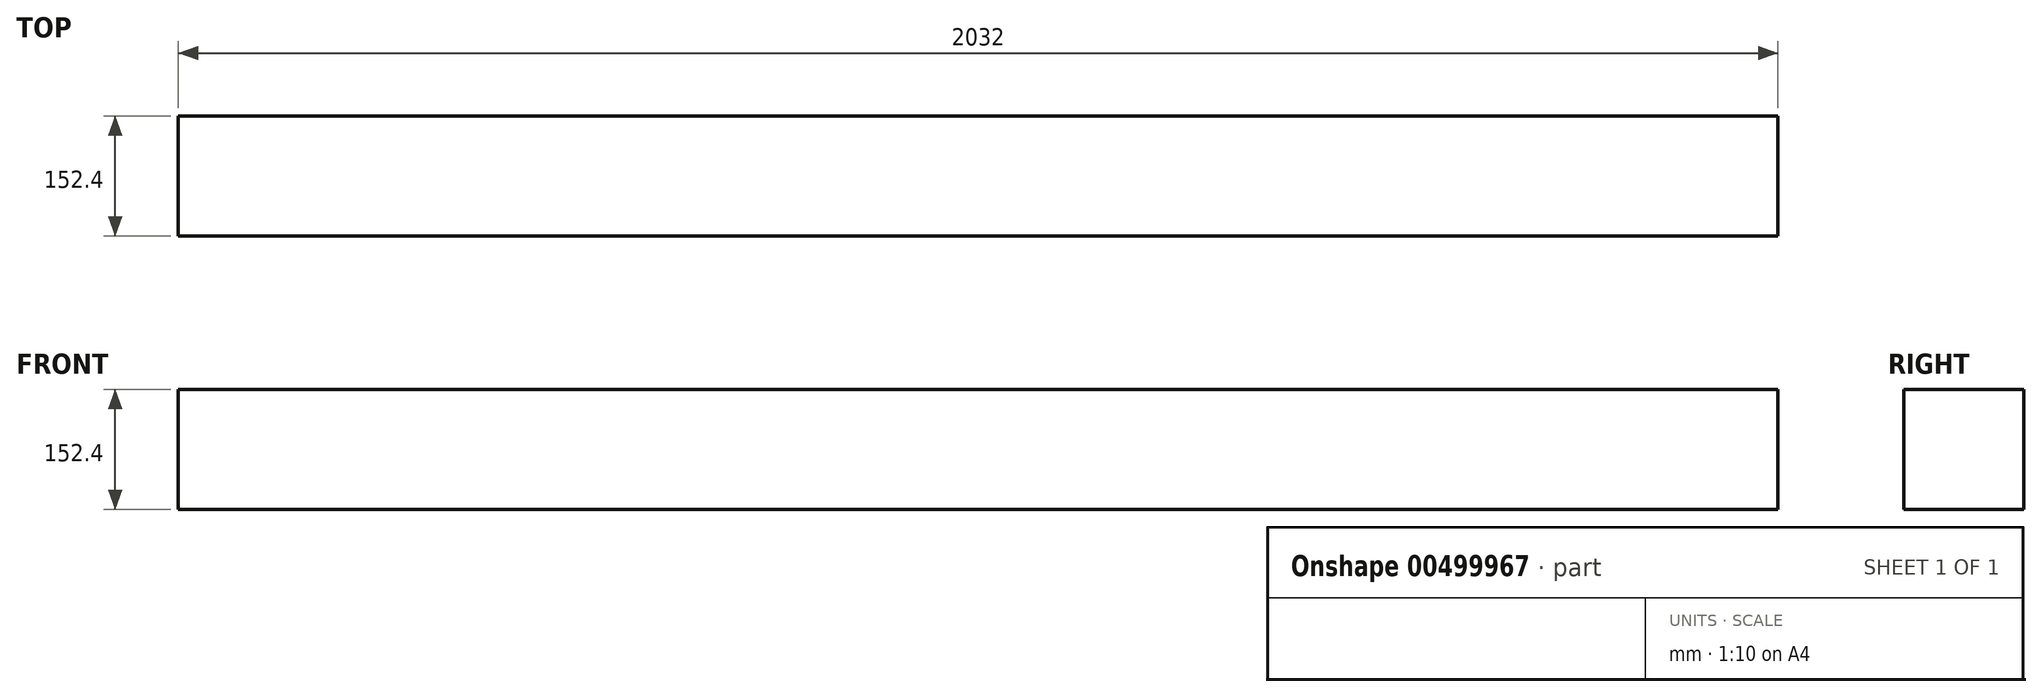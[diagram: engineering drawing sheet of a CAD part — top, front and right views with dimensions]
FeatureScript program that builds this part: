
annotation { "Feature Type Name" : "Feature", "Feature Type Description" : "" }
export const myFeature = defineFeature(function(context is Context, id is Id, definition is map)
    precondition{}
    {
        {
            var Q0;
            Q0=qCreatedBy(makeId("Front.planeOp"),FACE);
            var sketch = newSketch(context, id + "F0", { "sketchPlane" : qUnion([Q0])});
            skLineSegment(sketch, "E0.bottom", {"start": v(-1016, 76.2) * mm, "end": v(1016, 76.2) * mm});
            skLineSegment(sketch, "E0.top", {"start": v(-1016, -76.2) * mm, "end": v(1016, -76.2) * mm});
            skLineSegment(sketch, "E0.left", {"start": v(-1016, 76.2) * mm, "end": v(-1016, -76.2) * mm});
            skLineSegment(sketch, "E0.right", {"start": v(1016, 76.2) * mm, "end": v(1016, -76.2) * mm});
            skPoint(sketch, "E0.middle", {"position": v(0, 0) * mm});
            skSolve(sketch);
        }
        {
            var Q0;
            Q0 = qSketchRegion(id + "F0", true);
            extrude(context, id + "F1", {"entities" : qUnion([Q0]), "depth" : 152.4 * mm, "offsetDistance" : 25.4 * mm});
        }
    });
